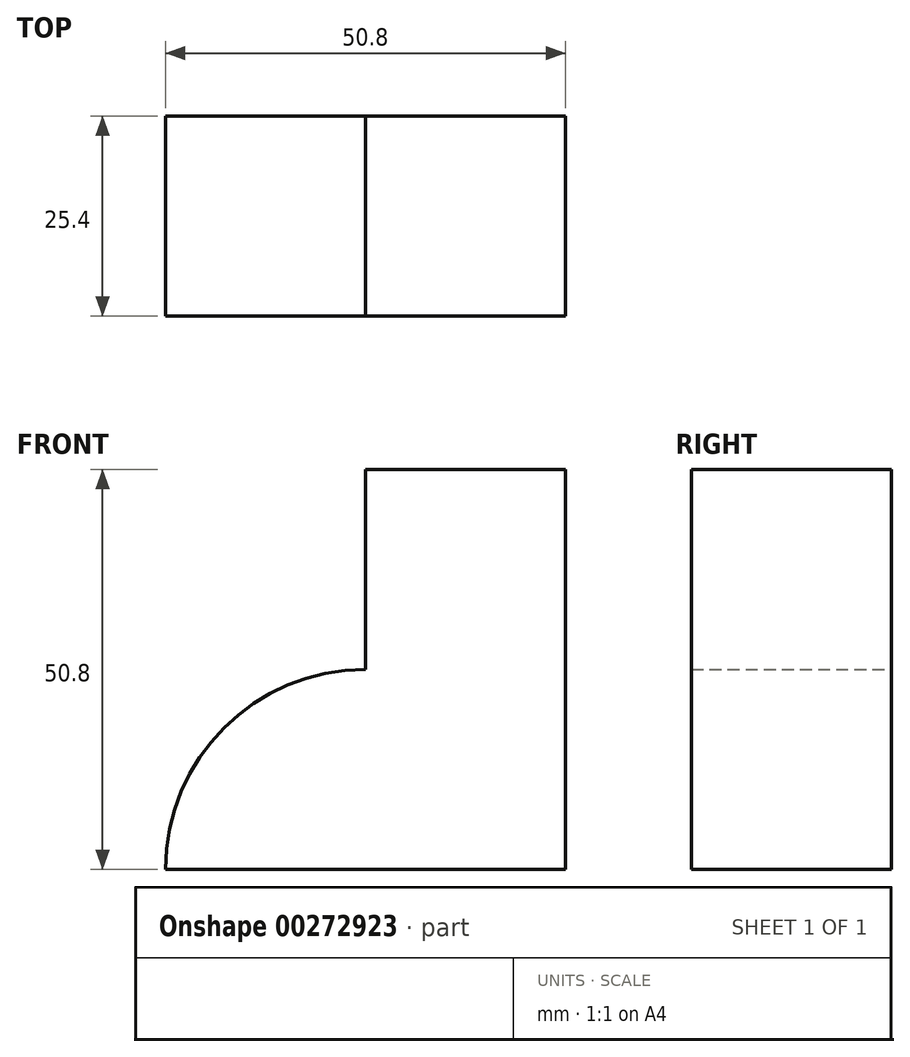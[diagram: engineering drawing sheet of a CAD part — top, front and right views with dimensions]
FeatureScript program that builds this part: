
annotation { "Feature Type Name" : "Feature", "Feature Type Description" : "" }
export const myFeature = defineFeature(function(context is Context, id is Id, definition is map)
    precondition{}
    {
        {
            var Q0;
            Q0=qCreatedBy(makeId("Front.planeOp"),FACE);
            var sketch = newSketch(context, id + "F0", { "sketchPlane" : qUnion([Q0])});
            skLineSegment(sketch, "E0", {"start": v(0, 0) * mm, "end": v(-50.8, 0) * mm});
            skLineSegment(sketch, "E1", {"start": v(0, 0) * mm, "end": v(0, 50.8) * mm});
            skLineSegment(sketch, "E2", {"start": v(0, 50.8) * mm, "end": v(-25.4, 50.8) * mm});
            skLineSegment(sketch, "E3", {"start": v(-25.4, 50.8) * mm, "end": v(-25.4, 25.4) * mm});
            skArc(sketch, "E4", {"start": v(-25.4, 25.4) * mm, "mid": v(-43.36, 17.96) * mm, "end": v(-50.8, 0) * mm});
            skSolve(sketch);
        }
        {
            var Q0;
            Q0=makeQuery(id+"F0.imprint","IMPRINT",FACE,{"disambiguationData":[TD([[makeQuery(id+"F0.imprint","IMPRINT",EDGE,{"derivedFrom":sQuery(id+"F0.wireOp",EDGE,"E0")}),-1.0]])]});
            extrude(context, id + "F1", {"entities" : qUnion([Q0]), "depth" : 25.4 * mm});
        }
    });
